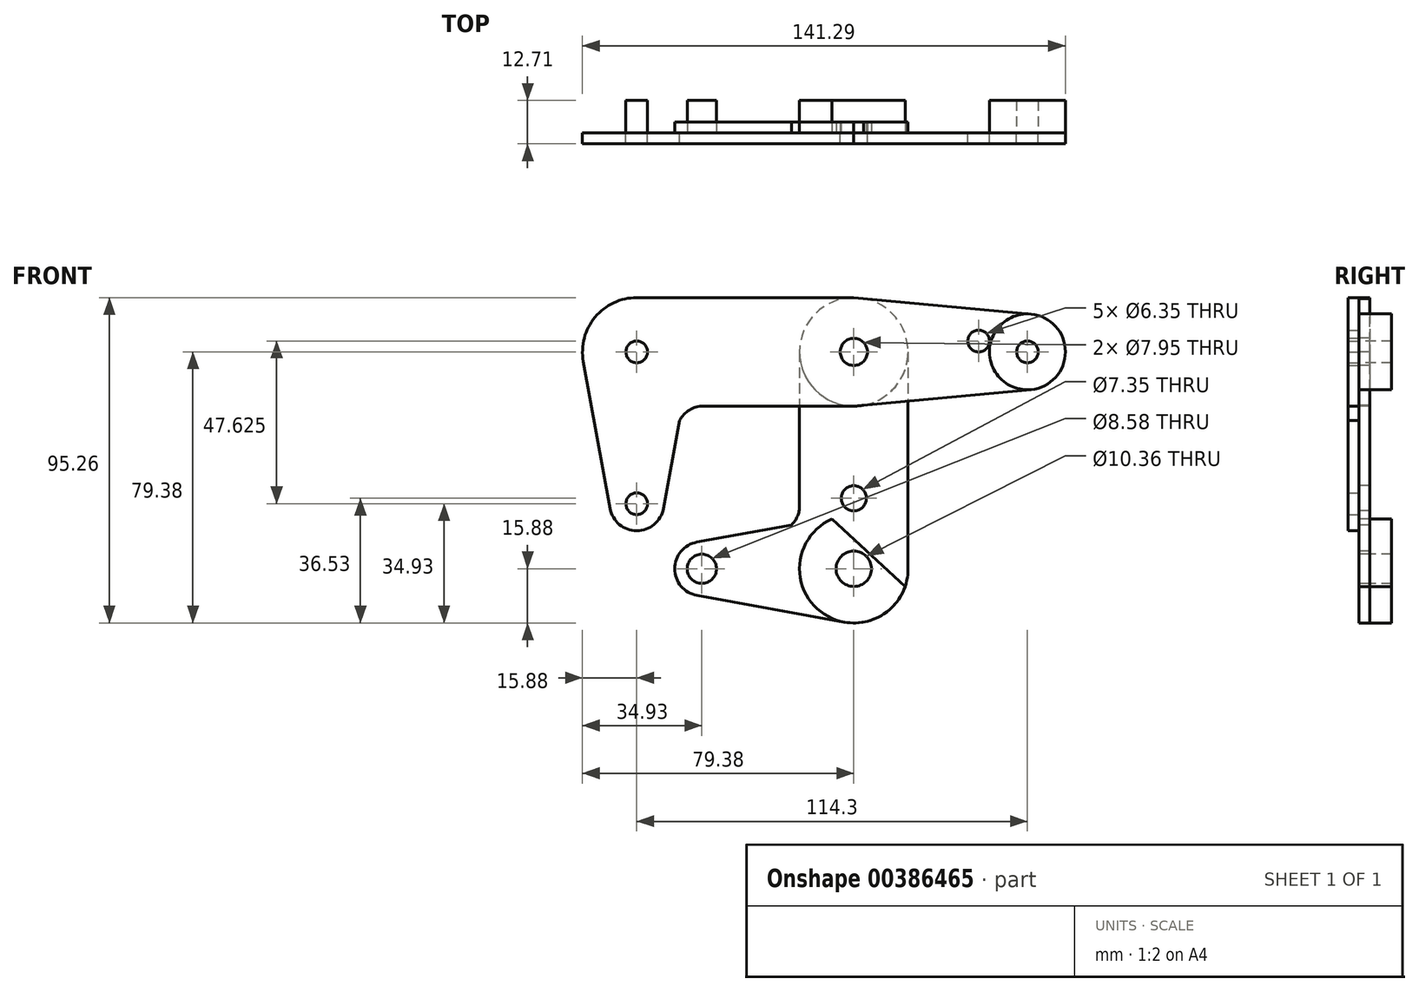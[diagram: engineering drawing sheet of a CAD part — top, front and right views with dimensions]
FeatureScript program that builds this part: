
annotation { "Feature Type Name" : "Feature", "Feature Type Description" : "" }
export const myFeature = defineFeature(function(context is Context, id is Id, definition is map)
    precondition{}
    {
        {
            var Q0;
            Q0=qCreatedBy(makeId("Front.planeOp"),FACE);
            var sketch = newSketch(context, id + "F0", { "sketchPlane" : qUnion([Q0])});
            skCircle(sketch, "E0", {"center": v(-63.5, 0) * mm, "radius": 3.18 * mm});
            skCircle(sketch, "E1", {"center": v(-63.5, 0) * mm, "radius": 15.88 * mm});
            skCircle(sketch, "E2", {"center": v(0, 0) * mm, "radius": 15.88 * mm});
            skCircle(sketch, "E3", {"center": v(0, 0) * mm, "radius": 3.98 * mm});
            skCircle(sketch, "E4", {"center": v(50.8, 0) * mm, "radius": 11.11 * mm});
            skCircle(sketch, "E5", {"center": v(50.8, 0) * mm, "radius": 3.18 * mm});
            skCircle(sketch, "E6", {"center": v(36.53, 3.18) * mm, "radius": 3.18 * mm});
            skCircle(sketch, "E7", {"center": v(-63.5, -44.45) * mm, "radius": 3.18 * mm});
            skCircle(sketch, "E8", {"center": v(-63.5, -44.45) * mm, "radius": 7.94 * mm});
            skLineSegment(sketch, "E9", {"start": v(-63.5, 0) * mm, "end": v(50.8, 0) * mm, "construction": true});
            skLineSegment(sketch, "E10", {"start": v(-63.5, 0) * mm, "end": v(-63.5, -44.45) * mm, "construction": true});
            skCircle(sketch, "E11", {"center": v(0, 0) * mm, "radius": 3.18 * mm});
            skLineSegment(sketch, "E12", {"start": v(-55.7, -45.87) * mm, "end": v(-51.02, -20.14) * mm});
            skLineSegment(sketch, "E13", {"start": v(0, -15.88) * mm, "end": v(-43.98, -15.88) * mm});
            skLineSegment(sketch, "E14", {"start": v(-63.5, 15.87) * mm, "end": v(0, 15.88) * mm});
            skLineSegment(sketch, "E15", {"start": v(0, -15.88) * mm, "end": v(51.83, -11.06) * mm});
            skLineSegment(sketch, "E16", {"start": v(0, 15.88) * mm, "end": v(51.83, 11.06) * mm});
            skArc(sketch, "E17", {"start": v(-43.98, -15.87) * mm, "mid": v(-48.1, -17.02) * mm, "end": v(-51.02, -20.14) * mm});
            skLineSegment(sketch, "E18", {"start": v(-79.12, -2.83) * mm, "end": v(-71.3, -45.87) * mm});
            skSolve(sketch);
        }
        {
            var Q0;
            Q0=qCreatedBy(makeId("Front.planeOp"),FACE);
            var sketch = newSketch(context, id + "F1", { "sketchPlane" : qUnion([Q0])});
            skLineSegment(sketch, "E19", {"start": v(0, 0) * mm, "end": v(0, -63.5) * mm, "construction": true});
            skCircle(sketch, "E20", {"center": v(0, -42.85) * mm, "radius": 3.68 * mm});
            skCircle(sketch, "E21", {"center": v(0, -63.5) * mm, "radius": 15.88 * mm});
            skCircle(sketch, "E22", {"center": v(0, -63.5) * mm, "radius": 5.18 * mm});
            skLineSegment(sketch, "E23", {"start": v(0, -63.5) * mm, "end": v(-44.45, -63.5) * mm, "construction": true});
            skCircle(sketch, "E24", {"center": v(-44.45, -63.5) * mm, "radius": 7.94 * mm});
            skCircle(sketch, "E25", {"center": v(-44.45, -63.5) * mm, "radius": 4.29 * mm});
            skLineSegment(sketch, "E26", {"start": v(15.88, 0) * mm, "end": v(15.88, -63.5) * mm});
            skLineSegment(sketch, "E27", {"start": v(-15.88, 0) * mm, "end": v(-15.87, -45.05) * mm});
            skLineSegment(sketch, "E28", {"start": v(-45.87, -71.3) * mm, "end": v(-2.83, -79.12) * mm});
            skLineSegment(sketch, "E29", {"start": v(-45.87, -55.7) * mm, "end": v(-18.2, -50.67) * mm});
            skArc(sketch, "E30", {"start": v(-18.2, -50.67) * mm, "mid": v(-16.48, -48.09) * mm, "end": v(-15.87, -45.05) * mm});
            skLineSegment(sketch, "E31", {"start": v(-63.48, -44.47) * mm, "end": v(-44.45, -63.5) * mm, "construction": true});
            skCircle(sketch, "E32.0", {"center": v(0, 0) * mm, "radius": 15.88 * mm});
            skSolve(sketch);
        }
        {
            var Q0;
            {var subQ0=sQuery(id+"F0.wireOp",EDGE,"E12");Q0=makeQuery(id+"F0.imprint","IMPRINT",FACE,{"disambiguationData":[TD([[makeQuery(id+"F0.imprint","IMPRINT",EDGE,{"derivedFrom":subQ0}),1.0]])]});}
            var Q1;
            Q1=makeQuery(id+"F0.imprint","IMPRINT",FACE,{"disambiguationData":[TD([[makeQuery(id+"F0.imprint","IMPRINT",EDGE,{"derivedFrom":sQuery(id+"F0.wireOp",EDGE,"E6")}),-1.0]])]});
            var Q2;
            Q2=makeQuery(id+"F0.imprint","IMPRINT",FACE,{"disambiguationData":[TD([[makeQuery(id+"F0.imprint","IMPRINT",EDGE,{"derivedFrom":sQuery(id+"F0.wireOp",EDGE,"E3")}),-1.0]])]});
            var Q3;
            Q3=makeQuery(id+"F0.imprint","IMPRINT",FACE,{"disambiguationData":[TD([[makeQuery(id+"F0.imprint","IMPRINT",EDGE,{"derivedFrom":sQuery(id+"F0.wireOp",EDGE,"E5")}),-1.0]])]});
            var Q4;
            Q4=makeQuery(id+"F0.imprint","IMPRINT",FACE,{"disambiguationData":[TD([[makeQuery(id+"F0.imprint","IMPRINT",EDGE,{"derivedFrom":sQuery(id+"F0.wireOp",EDGE,"E0")}),-1.0]])]});
            var Q5;
            Q5=makeQuery(id+"F0.imprint","IMPRINT",FACE,{"disambiguationData":[TD([[makeQuery(id+"F0.imprint","IMPRINT",EDGE,{"derivedFrom":sQuery(id+"F0.wireOp",EDGE,"E7")}),-1.0]])]});
            extrude(context, id + "F2", {"entities" : qUnion([Q0, Q1, Q2, Q3, Q4, Q5]), "depth" : 3.17 * mm});
        }
        {
            var Q0;
            Q0=makeQuery(id+"F1.imprint","IMPRINT",FACE,{"disambiguationData":[TD([[makeQuery(id+"F1.imprint","IMPRINT",EDGE,{"derivedFrom":sQuery(id+"F1.wireOp",EDGE,"E25")}),-1.0]])]});
            var Q1;
            Q1=makeQuery(id+"F1.imprint","IMPRINT",FACE,{"disambiguationData":[TD([[makeQuery(id+"F1.imprint","IMPRINT",EDGE,{"derivedFrom":sQuery(id+"F1.wireOp",EDGE,"E20")}),-1.0]])]});
            var Q2;
            Q2=makeQuery(id+"F1.imprint","IMPRINT",FACE,{"disambiguationData":[TD([[makeQuery(id+"F1.imprint","IMPRINT",EDGE,{"derivedFrom":sQuery(id+"F1.wireOp",EDGE,"E22")}),-1.0]])]});
            var Q3;
            Q3=makeQuery(id+"F0.imprint","IMPRINT",FACE,{"disambiguationData":[TD([[makeQuery(id+"F0.imprint","IMPRINT",EDGE,{"derivedFrom":sQuery(id+"F0.wireOp",EDGE,"E3")}),-1.0]])]});
            extrude(context, id + "F3", {"entities" : qUnion([Q0, Q1, Q2, Q3]), "oppositeDirection" : true, "depth" : 3.17 * mm});
        }
        {
            var Q0;
            Q0=makeQuery(id+"F1.imprint","IMPRINT",FACE,{"disambiguationData":[TD([[makeQuery(id+"F1.imprint","IMPRINT",EDGE,{"derivedFrom":sQuery(id+"F1.wireOp",EDGE,"E20")}),-1.0]])]});
            var sketch = newSketch(context, id + "F4", { "sketchPlane" : qUnion([Q0])});
            skCircle(sketch, "E33.0", {"center": v(0, -63.5) * mm, "radius": 15.88 * mm});
            skLineSegment(sketch, "E34.0.0", {"start": v(-18.2, -50.67) * mm, "end": v(-45.87, -55.7) * mm});
            skArc(sketch, "E34.0.1", {"start": v(-45.87, -55.7) * mm, "mid": v(-36.51, -63.5) * mm, "end": v(-45.87, -71.3) * mm});
            skLineSegment(sketch, "E34.0.2", {"start": v(-45.87, -71.3) * mm, "end": v(-2.83, -79.12) * mm});
            skArc(sketch, "E34.0.3", {"start": v(-2.83, -79.12) * mm, "mid": v(-10.17, -51.31) * mm, "end": v(15.88, -63.5) * mm});
            skLineSegment(sketch, "E34.0.4", {"start": v(15.88, -63.5) * mm, "end": v(15.88, 0) * mm});
            skArc(sketch, "E34.0.5", {"start": v(15.88, 0) * mm, "mid": v(0, -15.88) * mm, "end": v(-15.88, 0) * mm});
            skLineSegment(sketch, "E34.0.6", {"start": v(-15.88, 0) * mm, "end": v(-15.87, -45.05) * mm});
            skArc(sketch, "E34.0.7", {"start": v(-15.87, -45.05) * mm, "mid": v(-16.48, -48.09) * mm, "end": v(-18.2, -50.67) * mm});
            skLineSegment(sketch, "E35", {"start": v(0, -63.5) * mm, "end": v(50.73, 0) * mm, "construction": true});
            skLineSegment(sketch, "E36", {"start": v(-6.4, -48.98) * mm, "end": v(15, -68.68) * mm});
            skCircle(sketch, "E37.0", {"center": v(-44.45, -63.5) * mm, "radius": 4.29 * mm});
            skCircle(sketch, "E38.0", {"center": v(-63.5, 0) * mm, "radius": 3.18 * mm});
            skCircle(sketch, "E39.0", {"center": v(50.8, 0) * mm, "radius": 3.18 * mm});
            skCircle(sketch, "E40.0", {"center": v(0, 0) * mm, "radius": 3.98 * mm});
            skCircle(sketch, "E41.0", {"center": v(-63.5, -44.45) * mm, "radius": 3.18 * mm});
            skSolve(sketch);
        }
        {
            var Q0;
            Q0=qCreatedBy(makeId("Front.planeOp"),FACE);
            cPlane(context, id + "F5", {"entities" : qUnion([Q0]), "cplaneType" : CPlaneType.OFFSET, "offset" : 9.52 * mm, "oppositeDirection" : true, "width" : 152.4 * mm, "height" : 152.4 * mm});
        }
        {
            var Q0;
            {var subQ2=sQuery(id+"F4.wireOp",EDGE,"E36");Q0=makeQuery(id+"F4.imprint","IMPRINT",FACE,{"disambiguationData":[TD([[makeQuery(id+"F4.imprint","IMPRINT",EDGE,{"derivedFrom":subQ2}),-1.0]])]});}
            var Q1;
            Q1=makeQuery(id+"F1.imprint","IMPRINT",FACE,{"disambiguationData":[TD([[makeQuery(id+"F1.imprint","IMPRINT",EDGE,{"derivedFrom":sQuery(id+"F1.wireOp",EDGE,"E25")}),1.0]])]});
            var Q2;
            Q2=makeQuery(id+"F0.imprint","IMPRINT",FACE,{"disambiguationData":[TD([[makeQuery(id+"F0.imprint","IMPRINT",EDGE,{"derivedFrom":sQuery(id+"F0.wireOp",EDGE,"E0")}),1.0]])]});
            var Q3;
            Q3=makeQuery(id+"F0.imprint","IMPRINT",FACE,{"disambiguationData":[TD([[makeQuery(id+"F0.imprint","IMPRINT",EDGE,{"derivedFrom":sQuery(id+"F0.wireOp",EDGE,"E5")}),-1.0]])]});
            var Q4;
            Q4=qCreatedBy(id+"F5.planeOp",FACE);
            extrude(context, id + "F6", {"entities" : qUnion([Q0, Q1, Q2, Q3]), "endBound" : BoundingType.UP_TO_SURFACE, "oppositeDirection" : true, "endBoundEntityFace" : qUnion([Q4]), "depth" : 25.4 * mm});
        }
    });
